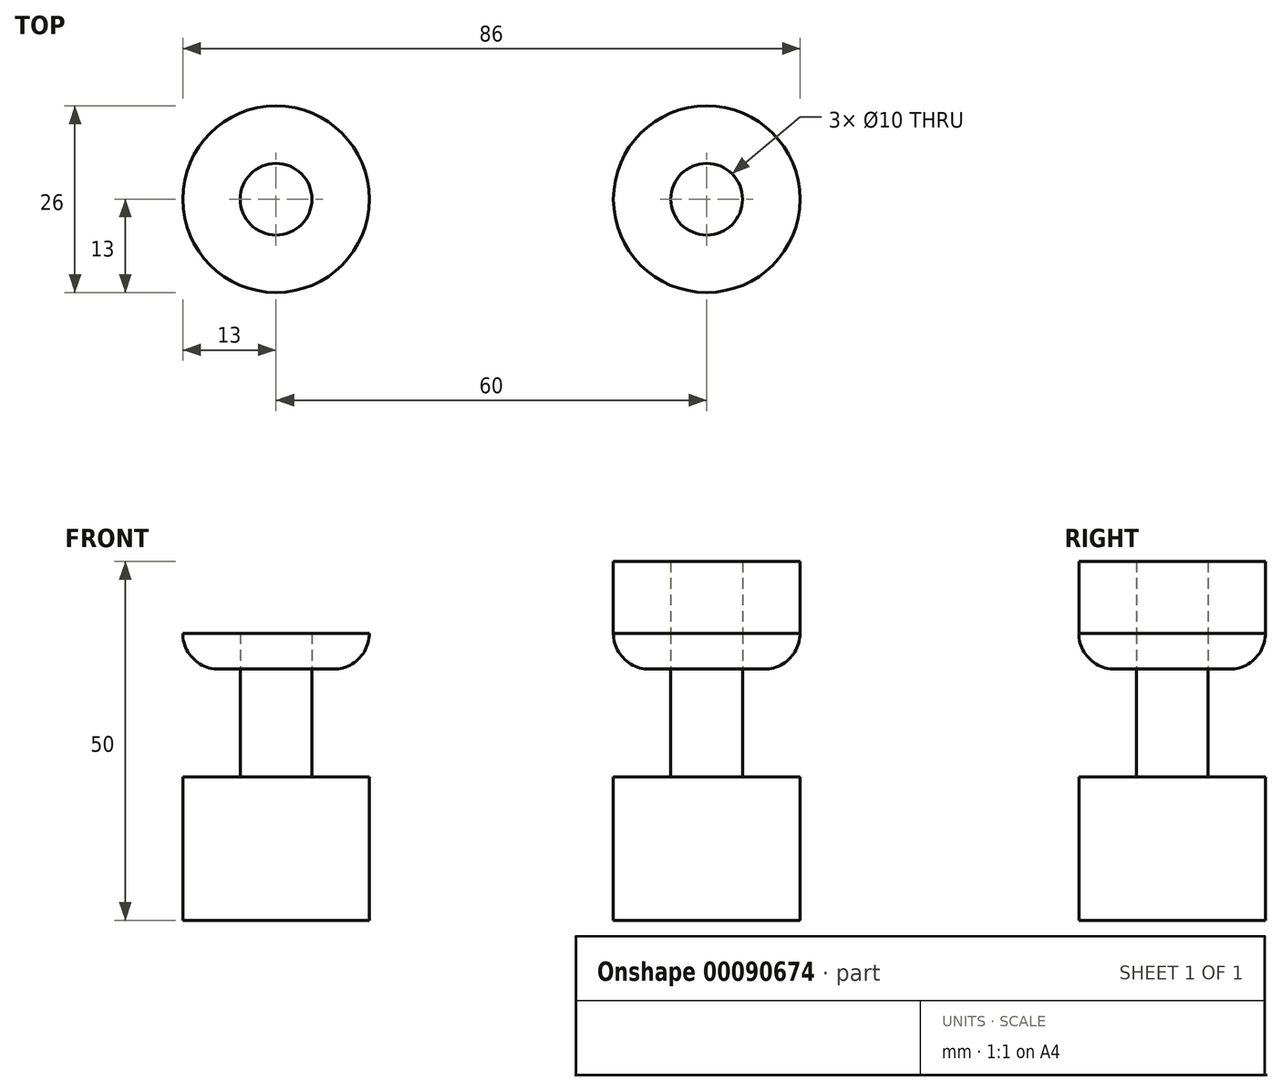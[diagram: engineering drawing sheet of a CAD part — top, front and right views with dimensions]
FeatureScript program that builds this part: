
annotation { "Feature Type Name" : "Feature", "Feature Type Description" : "" }
export const myFeature = defineFeature(function(context is Context, id is Id, definition is map)
    precondition{}
    {
        {
            var Q0;
            Q0=qCreatedBy(makeId("Top.planeOp"),FACE);
            var sketch = newSketch(context, id + "F0", { "sketchPlane" : qUnion([Q0])});
            skCircle(sketch, "E0", {"center": v(0, 0) * mm, "radius": 13 * mm});
            skSolve(sketch);
        }
        {
            var Q0;
            Q0=makeQuery(id+"F0.imprint","IMPRINT",FACE,{"disambiguationData":[TD([[makeQuery(id+"F0.imprint","IMPRINT",EDGE,{"derivedFrom":sQuery(id+"F0.wireOp",EDGE,"E0")}),1.0]])]});
            extrude(context, id + "F1", {"entities" : qUnion([Q0]), "depth" : 20 * mm});
        }
        {
            var Q0;
            Q0=makeQuery(id+"F1.opExtrude","CAP_FACE",FACE,{"disambiguationData":[OSD([sQuery(id+"F0.wireOp",EDGE,"E0")])],"isStart":false});
            var sketch = newSketch(context, id + "F2", { "sketchPlane" : qUnion([Q0])});
            skCircle(sketch, "E1", {"center": v(0, 0) * mm, "radius": 5 * mm});
            skSolve(sketch);
        }
        {
            var Q0;
            Q0=makeQuery(id+"F2.imprint","IMPRINT",FACE,{"disambiguationData":[TD([[makeQuery(id+"F2.imprint","IMPRINT",EDGE,{"derivedFrom":sQuery(id+"F2.wireOp",EDGE,"E1")}),1.0]])]});
            var Q1;
            Q1=sQuery(id+"F2.wireOp",EDGE,"E1");
            extrude(context, id + "F3", {"entities" : qUnion([Q0]), "operationType" : NewBodyOperationType.ADD, "surfaceEntities" : qUnion([Q1]), "depth" : 15 * mm});
        }
        {
            var Q0;
            Q0=makeQuery(id+"F3.opExtrude","CAP_FACE",FACE,{"disambiguationData":[OSD([sQuery(id+"F2.wireOp",EDGE,"E1")])],"isStart":false});
            var sketch = newSketch(context, id + "F4", { "sketchPlane" : qUnion([Q0])});
            skCircle(sketch, "E2", {"center": v(0, 0) * mm, "radius": 13 * mm});
            skSolve(sketch);
        }
        {
            var Q0;
            Q0=makeQuery(id+"F4.imprint","IMPRINT",FACE,{"disambiguationData":[TD([[makeQuery(id+"F4.imprint","IMPRINT",EDGE,{"derivedFrom":sQuery(id+"F4.wireOp",EDGE,"E2")}),1.0]])]});
            extrude(context, id + "F5", {"entities" : qUnion([Q0]), "depth" : 5 * mm});
        }
        {
            var Q0;
            Q0=makeQuery(id+"F3.opExtrude","CAP_FACE",FACE,{"disambiguationData":[OSD([sQuery(id+"F2.wireOp",EDGE,"E1")])],"isStart":false});
            extrude(context, id + "F6", {"entities" : qUnion([Q0]), "depth" : 5 * mm});
        }
        {
            var Q0;
            Q0=makeQuery(id+"F5.opExtrude","CAP_EDGE",EDGE,{"disambiguationData":[OSD([sQuery(id+"F4.wireOp",EDGE,"E2")])],"isStart":true});
            fillet(context, id + "F7", {"entities" : qUnion([Q0]), "radius" : 5 * mm, "tangentPropagation" : true, "allowEdgeOverflow" : false});
        }
        {
            var Q0;
            Q0=makeQuery(id+"F1.opExtrude","SWEPT_BODY",BODY,{"disambiguationData":[OSD([sQuery(id+"F0.wireOp",EDGE,"E0")])]});
            var Q1;
            Q1=makeQuery(id+"F5.opExtrude","SWEPT_BODY",BODY,{"disambiguationData":[OSD([sQuery(id+"F2.wireOp",EDGE,"E1"),sQuery(id+"F4.wireOp",EDGE,"E2")])]});
            var Q2;
            Q2=makeQuery(id+"F6.opExtrude","SWEPT_BODY",BODY,{"disambiguationData":[OSD([sQuery(id+"F2.wireOp",EDGE,"E1")])]});
            transform(context, id + "F8", {"entities" : qUnion([Q0, Q1, Q2]), "transformType" : TransformType.TRANSLATION_3D, "dx" : 60 * mm, "dy" : 0 * mm, "dz" : 0 * mm, "makeCopy" : true});
        }
        {
            var Q0;
            Q0=makeQuery(id+"F8.opPattern","COPY",FACE,{"derivedFrom":makeQuery(id+"F5.opExtrude","CAP_FACE",FACE,{"disambiguationData":[OSD([sQuery(id+"F2.wireOp",EDGE,"E1"),sQuery(id+"F4.wireOp",EDGE,"E2")])],"isStart":false}),"instanceName":"1"});
            var Q1;
            Q1=makeQuery(id+"F8.opPattern","COPY",FACE,{"derivedFrom":makeQuery(id+"F6.opExtrude","CAP_FACE",FACE,{"disambiguationData":[OSD([sQuery(id+"F2.wireOp",EDGE,"E1")])],"isStart":false}),"instanceName":"1"});
            extrude(context, id + "F9", {"entities" : qUnion([Q0, Q1]), "depth" : 10 * mm});
        }
    });
